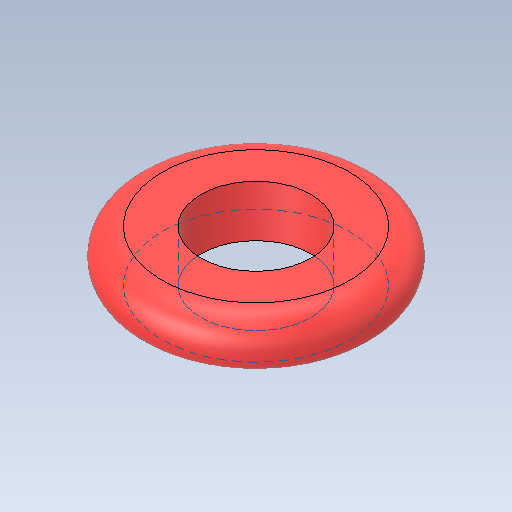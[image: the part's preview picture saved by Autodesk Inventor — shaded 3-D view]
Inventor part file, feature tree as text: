
AUTODESK INVENTOR PART (.ipt)
format: ipt  version: 2020 (Build 240168000, 168)  size: 143,360 bytes
history: native  units: mm
features: other x1, extrude x1, fillet x1, sketch x1
ambient origin geometry x8: Origin, YZ Plane, XZ Plane, XY Plane, X Axis, Y Axis, Z Axis, Center Point
bodies: Body1 (feature_tree)
feature tree (4):
  other  "ソリッド1"
  extrude  "押し出し1"  Depth=6.5mm
  fillet  "フィレット1"  Radius=3.0mm
  sketch  "スケッチ1"
